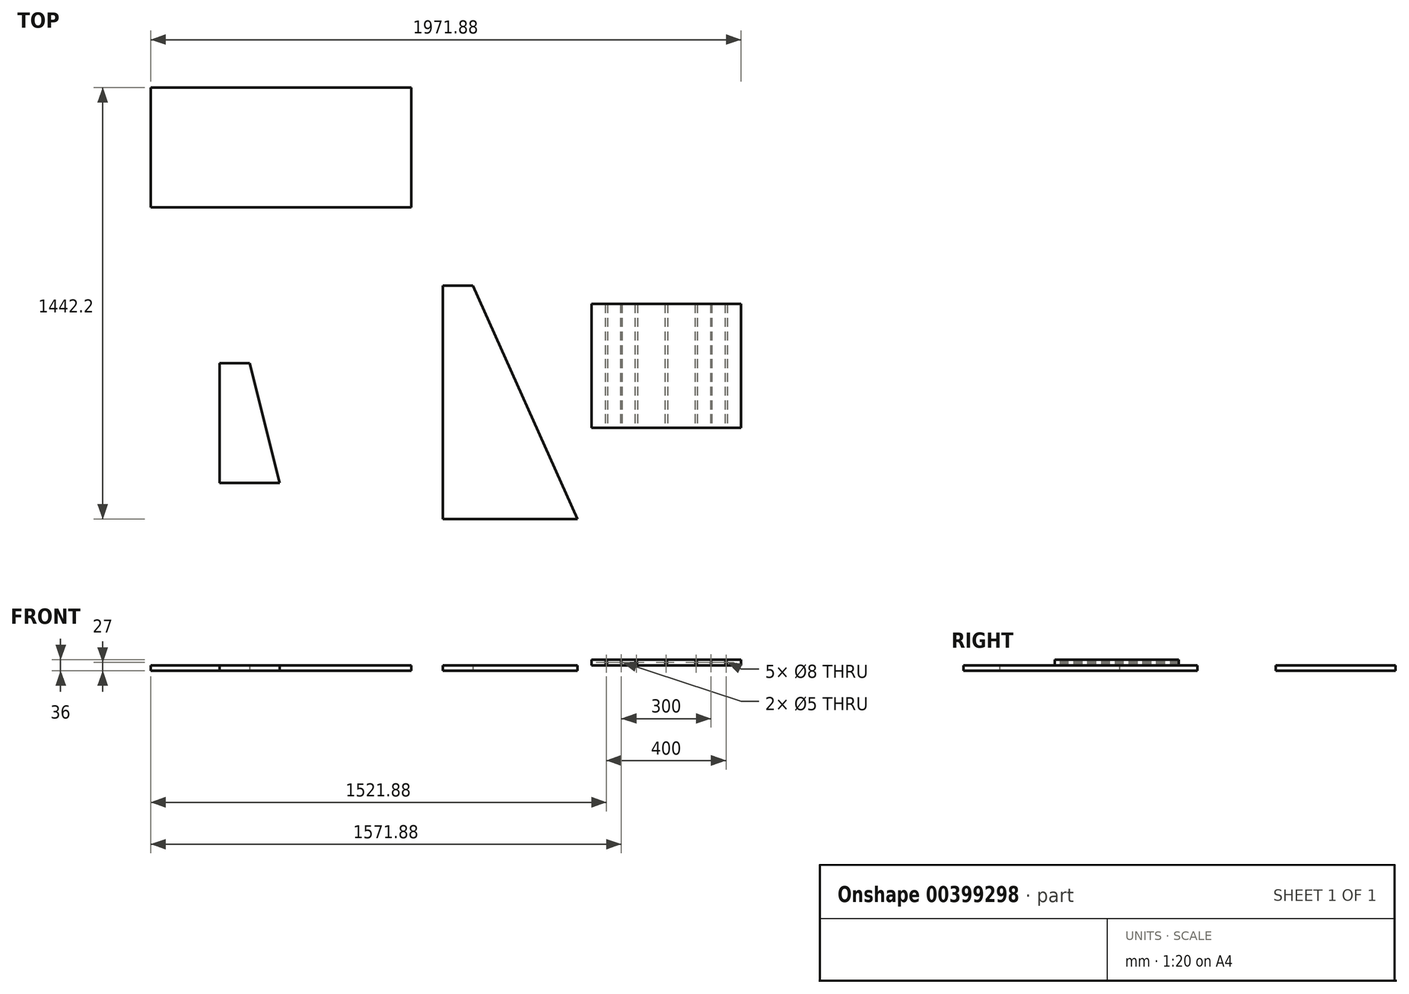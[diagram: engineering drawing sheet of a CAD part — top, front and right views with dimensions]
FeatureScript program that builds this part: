
annotation { "Feature Type Name" : "Feature", "Feature Type Description" : "" }
export const myFeature = defineFeature(function(context is Context, id is Id, definition is map)
    precondition{}
    {
        {
            var Q0;
            Q0=qCreatedBy(makeId("Top.planeOp"),FACE);
            var sketch = newSketch(context, id + "F0", { "sketchPlane" : qUnion([Q0])});
            skLineSegment(sketch, "E0.bottom", {"start": v(-196.07, -304.6) * mm, "end": v(253.93, -304.6) * mm});
            skLineSegment(sketch, "E0.top", {"start": v(-196.07, 475.4) * mm, "end": v(-96.07, 475.4) * mm});
            skLineSegment(sketch, "E0.left", {"start": v(-196.07, -304.6) * mm, "end": v(-196.07, 475.4) * mm});
            skLineSegment(sketch, "E0.right", {"start": v(253.93, -304.6) * mm, "end": v(-96.07, 475.4) * mm});
            skSolve(sketch);
        }
        {
            var Q0;
            Q0=qSketchRegion(id+"F0",true);
            extrude(context, id + "F1", {"entities" : qUnion([Q0]), "depth" : 18 * mm});
        }
        {
            var Q0;
            Q0=makeQuery(id+"F1.opExtrude","CAP_FACE",FACE,{"disambiguationData":[OSD([sQuery(id+"F0.wireOp",EDGE,"E0.bottom"),sQuery(id+"F0.wireOp",EDGE,"E0.top"),sQuery(id+"F0.wireOp",EDGE,"E0.left"),sQuery(id+"F0.wireOp",EDGE,"E0.right")])],"isStart":false});
            var sketch = newSketch(context, id + "F2", { "sketchPlane" : qUnion([Q0])});
            skLineSegment(sketch, "E1.bottom", {"start": v(300, 414) * mm, "end": v(800, 414) * mm});
            skLineSegment(sketch, "E1.top", {"start": v(300, 0) * mm, "end": v(800, 0) * mm});
            skLineSegment(sketch, "E1.left", {"start": v(300, 414) * mm, "end": v(300, 0) * mm});
            skLineSegment(sketch, "E1.right", {"start": v(800, 414) * mm, "end": v(800, 0) * mm});
            skLineSegment(sketch, "E2", {"start": v(0, 0) * mm, "end": v(300, 0) * mm, "construction": true});
            skSolve(sketch);
        }
        {
            var Q0;
            {var subQ1=sQuery(id+"F2.wireOp",EDGE,"E1.bottom");Q0=makeQuery(id+"F2.imprint","IMPRINT",FACE,{"disambiguationData":[TD([[makeQuery(id+"F2.imprint","IMPRINT",EDGE,{"derivedFrom":subQ1}),-1.0]])]});}
            extrude(context, id + "F3", {"entities" : qUnion([Q0]), "depth" : 18 * mm});
        }
        {
            var Q0;
            Q0=qSketchRegion(id+"F2",true);
            extrude(context, id + "F4", {"entities" : qUnion([Q0]), "operationType" : NewBodyOperationType.ADD, "depth" : 18 * mm});
        }
        {
            var Q0;
            Q0=makeQuery(id+"F3.opExtrude","SWEPT_FACE",FACE,{"disambiguationData":[OSD([sQuery(id+"F2.wireOp",EDGE,"E1.top")])]});
            var sketch = newSketch(context, id + "F5", { "sketchPlane" : qUnion([Q0])});
            skLineSegment(sketch, "E3", {"start": v(300, 27) * mm, "end": v(800, 27) * mm, "construction": true});
            skPoint(sketch, "E4", {"position": v(350, 27) * mm});
            skPoint(sketch, "E5.1.0.0", {"position": v(450, 27) * mm});
            skPoint(sketch, "E5.2.0.0", {"position": v(550, 27) * mm});
            skPoint(sketch, "E5.3.0.0", {"position": v(650, 27) * mm});
            skPoint(sketch, "E5.4.0.0", {"position": v(750, 27) * mm});
            skLineSegment(sketch, "E5.direction1", {"start": v(350, 27) * mm, "end": v(450, 27) * mm, "construction": true});
            skPoint(sketch, "E6", {"position": v(400, 27) * mm});
            skPoint(sketch, "E7", {"position": v(700, 27) * mm});
            skSolve(sketch);
        }
        {
            var Q0;
            Q0=sQuery(id+"F5.wireOp",VERTEX,"E4");
            var Q1;
            Q1=sQuery(id+"F5.wireOp",VERTEX,"E5.1.0.0");
            var Q2;
            Q2=sQuery(id+"F5.wireOp",VERTEX,"E5.2.0.0");
            var Q3;
            Q3=sQuery(id+"F5.wireOp",VERTEX,"E5.3.0.0");
            var Q4;
            Q4=sQuery(id+"F5.wireOp",VERTEX,"E5.4.0.0");
            var Q5;
            Q5=makeQuery(id+"F3.opExtrude","SWEPT_BODY",BODY,{"disambiguationData":[OSD([sQuery(id+"F2.wireOp",EDGE,"E1.bottom"),sQuery(id+"F2.wireOp",EDGE,"E1.top"),sQuery(id+"F2.wireOp",EDGE,"E1.left"),sQuery(id+"F2.wireOp",EDGE,"E1.right")])]});
            hole(context, id + "F6", {"style" : HoleStyle.SIMPLE, "endStyle" : HoleEndStyle.THROUGH, "holeDiameter" : 8 * mm, "isTappedThrough" : true, "tappedDepth" : 12 * mm, "tapClearance" : 3, "startFromSketch" : true, "locations" : qUnion([Q0, Q1, Q2, Q3, Q4]), "scope" : qUnion([Q5])});
        }
        {
            var Q0;
            Q0=qCreatedBy(makeId("Top.planeOp"),FACE);
            var sketch = newSketch(context, id + "F7", { "sketchPlane" : qUnion([Q0])});
            skLineSegment(sketch, "E8", {"start": v(-941.01, -183.88) * mm, "end": v(-941.01, 216.12) * mm});
            skLineSegment(sketch, "E9", {"start": v(-941.01, 216.12) * mm, "end": v(-841.01, 216.12) * mm});
            skLineSegment(sketch, "E10", {"start": v(-841.01, 216.12) * mm, "end": v(-741.01, -183.88) * mm});
            skLineSegment(sketch, "E11", {"start": v(-741.01, -183.88) * mm, "end": v(-941.01, -183.88) * mm});
            skSolve(sketch);
        }
        {
            var Q0;
            Q0=qSketchRegion(id+"F7",true);
            extrude(context, id + "F8", {"entities" : qUnion([Q0]), "depth" : 18 * mm});
        }
        {
            var Q0;
            Q0=qCreatedBy(makeId("Top.planeOp"),FACE);
            var sketch = newSketch(context, id + "F9", { "sketchPlane" : qUnion([Q0])});
            skLineSegment(sketch, "E12.bottom", {"start": v(-1171.88, 1137.6) * mm, "end": v(-301.88, 1137.6) * mm});
            skLineSegment(sketch, "E12.top", {"start": v(-1171.88, 737.6) * mm, "end": v(-301.88, 737.6) * mm});
            skLineSegment(sketch, "E12.left", {"start": v(-1171.88, 1137.6) * mm, "end": v(-1171.88, 737.6) * mm});
            skLineSegment(sketch, "E12.right", {"start": v(-301.88, 1137.6) * mm, "end": v(-301.88, 737.6) * mm});
            skSolve(sketch);
        }
        {
            var Q0;
            Q0=makeQuery(id+"F9.imprint","IMPRINT",FACE,{"disambiguationData":[TD([[makeQuery(id+"F9.imprint","IMPRINT",EDGE,{"derivedFrom":sQuery(id+"F9.wireOp",EDGE,"E12.bottom")}),-1.0]])]});
            extrude(context, id + "F10", {"entities" : qUnion([Q0]), "depth" : 18 * mm});
        }
        {
            var Q0;
            Q0=sQuery(id+"F5.wireOp",VERTEX,"E6");
            var Q1;
            Q1=sQuery(id+"F5.wireOp",VERTEX,"E7");
            var Q2;
            Q2=makeQuery(id+"F3.opExtrude","SWEPT_BODY",BODY,{"disambiguationData":[OSD([sQuery(id+"F2.wireOp",EDGE,"E1.bottom"),sQuery(id+"F2.wireOp",EDGE,"E1.top"),sQuery(id+"F2.wireOp",EDGE,"E1.left"),sQuery(id+"F2.wireOp",EDGE,"E1.right")])]});
            hole(context, id + "F11", {"style" : HoleStyle.SIMPLE, "endStyle" : HoleEndStyle.THROUGH, "holeDiameter" : 5 * mm, "isTappedThrough" : true, "tappedDepth" : 12 * mm, "tapClearance" : 3, "startFromSketch" : true, "locations" : qUnion([Q0, Q1]), "scope" : qUnion([Q2])});
        }
    });
